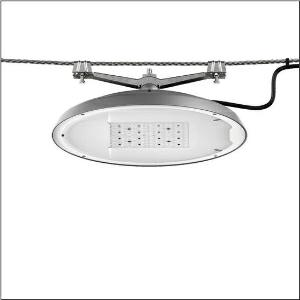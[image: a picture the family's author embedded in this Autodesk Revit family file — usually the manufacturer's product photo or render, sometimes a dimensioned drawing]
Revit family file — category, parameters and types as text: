
# Revit family: dl_r__50_iq_mini___st0_8s_5xa248v41f08me_8e0e
name_source: partatom
category: Lighting Fixtures
units: mm (PartAtom-declared; Revit-internal decimal feet)

## family parameters
Cut with Voids When Loaded = No
Host = Face
Light Source = No
Part Type = Normal
Room Calculation Point = No
Round Connector Dimension = Use Diameter
Shared = No

## types (1)
- --- (1 x LED, 15660 lm, 101.7 W, 4000K)
    Apparent Load = 102 VA
    CIE Flux Codes = 38 75 97 100 100
    Color Rendering = 70
    Color Temperature = 4000K
    Default Elevation = 1800 mm
    Description = DL® 50 iQ mini, catenary luminaire, primary light control with lens, of PMMA, primary optical cover: cover, of toughened safety glass, transparent, light distribution: ST0.8s, light emission: direct distribution, primary light characteristic: symmetric, installation type: suspended mounting, LED, High Power LED, rated luminous flux: 15.660lm, luminous efficacy: 154lm/W, light colour: 740, colour temperature: 4000K, control: optimised constant luminous flux control (CLO 2.0), Desk-Remote (wireless, voltage-free reading and setting of iQ features in the workshop via application-optimized NFC function/RFID function), Light-Fading, Smart-Wire, Night-Set, Lumen-Switch, Temp-Guard, Auto-Match, Street-Remote, mains connection: 230..240V, AC, 50/60Hz, start of lifetime: 102W, end of service life: 111W, reduction: 45W, luminaire housing, of diecast aluminium, powder-coated, Siteco® metallic grey (DB 702S), diameter: 500mm, height: 115mm, protection rating (complete): IP66, insulation class (complete): insulation class II (safety insulation), certification: CE, ENEC, VDE, impact resistance: IK08, permissible operating ambient temperature for outdoor applications: -25..+40°C, standard-compliant lighting for roads and squares, packaging unit: 1 piece

Light Distribution: ST0.8s
    Height = 124 mm  [stored 0.406824 ft]
    Lamp = 1 x LED
    Lamp Light Flux = 15660 lm
    Lamp Power = 101.7 W
    Lamp count = 1
    Length = 500 mm
    Luminous efficacy = 154 lm/W
    Manufacturer = Siteco
    ModVariant = No
    Model = 5XA248V41F08ME
    Number of Poles = 1
    OnlyDefault = Yes
    Power Factor = 1
    Product Name = DL® 50 iQ mini | ST0.8s
    Product group = catenary luminaire
    ProductGroupID = 6300
    Protection Class = Protection class II
    Protection Degree = IP 66
    RLX_Detail_Level = 1
    RLX_Emergency_Light_Flux = 0 lm
    RLX_Emergency_Type = 0
    RLX_Emergency_Type_DB = No
    RlxData = <blob elided: 127061 chars, md5=6342dfb9>
    Socket = socket
    Standby Power = 0 W
    System Light Flux = 15660 lm
    System Power = 102 W
    Type Comments = factory setting: luminous flux: 100 % | dim-lin: 254 | 534 mA
    Type Image = l_1251783.jpg
    URL = http://relux.com
    VarID = @adj_072269
    Voltage = 0 V
    Weight = 0.00 kg
    Width = 0 mm  [stored 0 ft]

note: [stored X ft] marks values corroborated as IEEE doubles in the binary element streams (Revit-internal decimal feet)

## geometry (parser evidence)
native form markers: Blend x4, Sweep x15
no freeform markers — native parametric forms only
